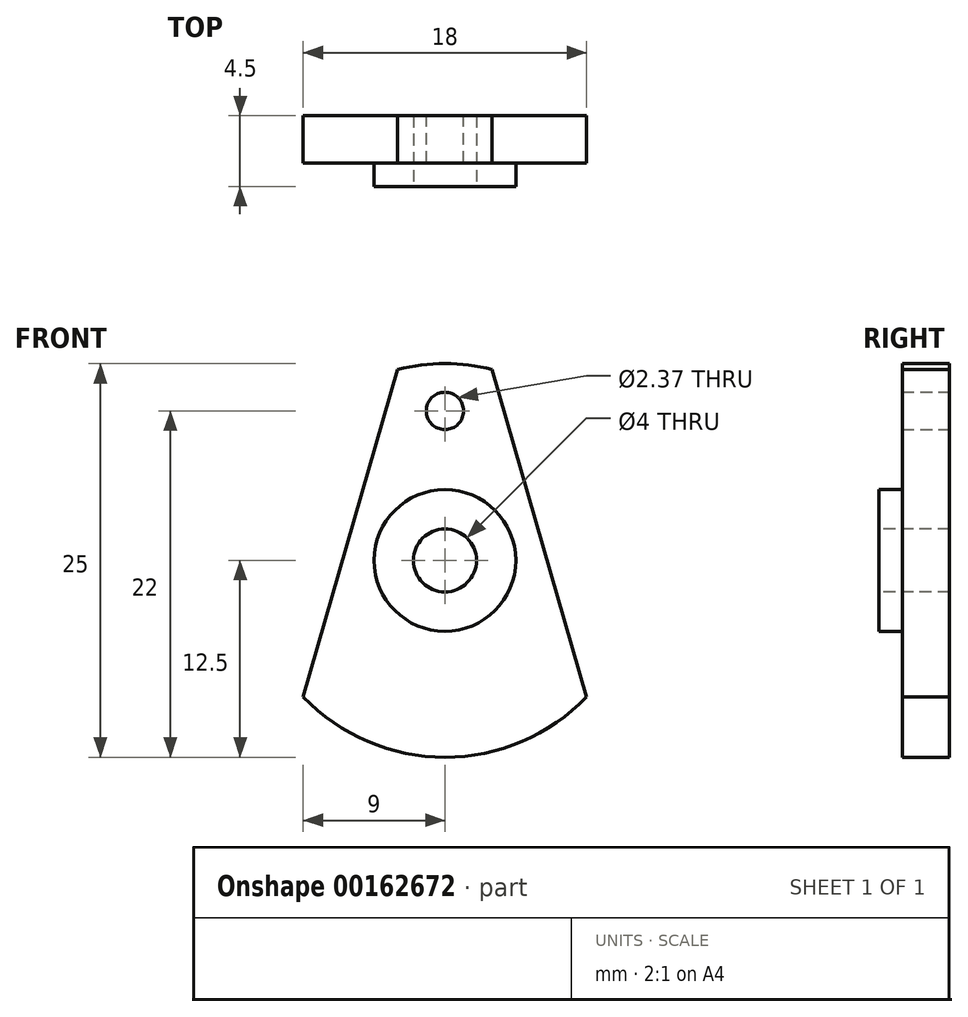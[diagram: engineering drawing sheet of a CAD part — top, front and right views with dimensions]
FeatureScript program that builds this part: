
annotation { "Feature Type Name" : "Feature", "Feature Type Description" : "" }
export const myFeature = defineFeature(function(context is Context, id is Id, definition is map)
    precondition{}
    {
        {
            var Q0;
            Q0=qCreatedBy(makeId("Front.planeOp"),FACE);
            var sketch = newSketch(context, id + "F0", { "sketchPlane" : qUnion([Q0])});
            skArc(sketch, "E0", {"start": v(-9, -8.67) * mm, "mid": v(0, -12.5) * mm, "end": v(9, -8.67) * mm});
            skLineSegment(sketch, "E1", {"start": v(-3, 12.13) * mm, "end": v(-9, -8.67) * mm});
            skLineSegment(sketch, "E2.MirrorCS", {"start": v(3, 12.13) * mm, "end": v(9, -8.67) * mm});
            skCircle(sketch, "E3", {"center": v(0, 9.5) * mm, "radius": 1.19 * mm});
            skCircle(sketch, "E4", {"center": v(0, 0) * mm, "radius": 4.5 * mm});
            skArc(sketch, "E5.trimOffspring", {"start": v(3, 12.13) * mm, "mid": v(0, 12.5) * mm, "end": v(-3, 12.13) * mm});
            skPoint(sketch, "E6.orphan", {"position": v(0, 12.5) * mm});
            skLineSegment(sketch, "E7", {"start": v(0, 2.05) * mm, "end": v(0, -2.08) * mm, "construction": true});
            skLineSegment(sketch, "E8", {"start": v(-1.78, 0) * mm, "end": v(1.7, 0) * mm, "construction": true});
            skSolve(sketch);
        }
        {
            var Q0;
            Q0 = qSketchRegion(id + "F0", true);
            var Q1;
            Q1=makeQuery(id+"F0.imprint","IMPRINT",FACE,{"disambiguationData":[TD([[makeQuery(id+"F0.imprint","IMPRINT",EDGE,{"derivedFrom":sQuery(id+"F0.wireOp",EDGE,"E4")}),1.0]])]});
            extrude(context, id + "F1", {"entities" : qUnion([Q0, Q1]), "depth" : 3 * mm, "offsetDistance" : 25 * mm});
        }
        {
            var Q0;
            Q0=makeQuery(id+"F0.imprint","IMPRINT",FACE,{"disambiguationData":[TD([[makeQuery(id+"F0.imprint","IMPRINT",EDGE,{"derivedFrom":sQuery(id+"F0.wireOp",EDGE,"E4")}),1.0]])]});
            extrude(context, id + "F2", {"entities" : qUnion([Q0]), "operationType" : NewBodyOperationType.ADD, "depth" : 4.5 * mm, "offsetDistance" : 25 * mm});
        }
        {
            var Q0;
            Q0=makeQuery(id+"F1.opExtrude","CAP_FACE",FACE,{"disambiguationData":[OSD([sQuery(id+"F0.wireOp",EDGE,"E0"),sQuery(id+"F0.wireOp",EDGE,"E1"),sQuery(id+"F0.wireOp",EDGE,"E2.MirrorCS"),sQuery(id+"F0.wireOp",EDGE,"E3"),sQuery(id+"F0.wireOp",EDGE,"E5.trimOffspring")])],"isStart":true});
            var sketch = newSketch(context, id + "F3", { "sketchPlane" : qUnion([Q0])});
            skLineSegment(sketch, "E9", {"start": v(0, 2.88) * mm, "end": v(0, 0) * mm, "construction": true});
            skLineSegment(sketch, "E10", {"start": v(-2.34, 0) * mm, "end": v(0, 0) * mm, "construction": true});
            skSolve(sketch);
        }
        {
            var Q0;
            Q0=sQuery(id+"F3.wireOp",VERTEX,"E10.end");
            var Q1;
            Q1=makeQuery(id+"F1.opExtrude","SWEPT_BODY",BODY,{"disambiguationData":[OSD([sQuery(id+"F0.wireOp",EDGE,"E0"),sQuery(id+"F0.wireOp",EDGE,"E1"),sQuery(id+"F0.wireOp",EDGE,"E2.MirrorCS"),sQuery(id+"F0.wireOp",EDGE,"E3"),sQuery(id+"F0.wireOp",EDGE,"E5.trimOffspring")])]});
            hole(context, id + "F4", {"style" : HoleStyle.SIMPLE, "endStyle" : HoleEndStyle.THROUGH, "standardTappedOrClearance" : lookupTablePath({ "standard" : "ISO", "size" : "4", "type" : "Drilled" }), "standardBlindInLast" : lookupTablePath({ "standard" : "ISO", "size" : "4", "type" : "Drilled" }), "holeDiameter" : 4 * mm, "isTappedThrough" : true, "tappedDepth" : 12 * mm, "tapClearance" : 3, "locations" : qUnion([Q0]), "scope" : qUnion([Q1]), "majorDiameter" : 4 * mm, "startStyle" : HoleStartStyle.PART});
        }
    });
